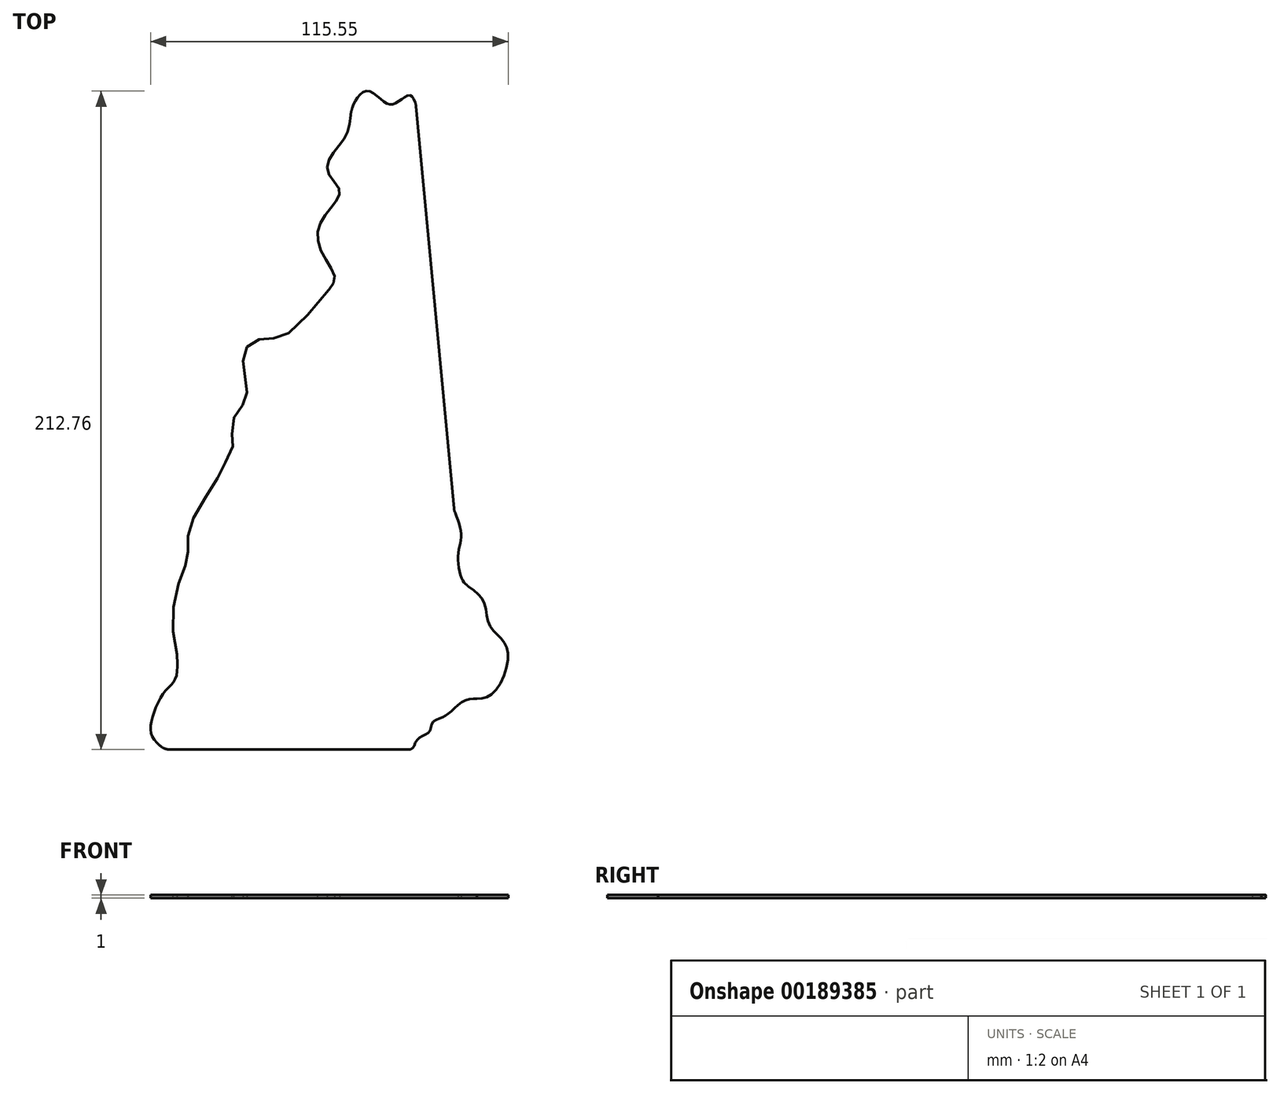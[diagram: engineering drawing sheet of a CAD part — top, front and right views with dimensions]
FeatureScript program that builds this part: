
annotation { "Feature Type Name" : "Feature", "Feature Type Description" : "" }
export const myFeature = defineFeature(function(context is Context, id is Id, definition is map)
    precondition{}
    {
        {
            var Q0;
            Q0=qCreatedBy(makeId("Top.planeOp"),FACE);
            var sketch = newSketch(context, id + "F0", { "sketchPlane" : qUnion([Q0])});
            skLineSegment(sketch, "E0.bottom", {"start": v(114, -114) * mm, "end": v(-114, -114) * mm});
            skLineSegment(sketch, "E0.top", {"start": v(114, 114) * mm, "end": v(-114, 114) * mm});
            skLineSegment(sketch, "E0.left", {"start": v(114, -114) * mm, "end": v(114, 114) * mm});
            skLineSegment(sketch, "E0.right", {"start": v(-114, -114) * mm, "end": v(-114, 114) * mm});
            skPoint(sketch, "E0.middle", {"position": v(0, 0) * mm});
            skSolve(sketch);
        }
        {
            var Q0;
            Q0 = qSketchRegion(id + "F0", true);
            extrude(context, id + "F1", {"entities" : qUnion([Q0]), "depth" : 1 * mm});
        }
        {
            var Q0;
            Q0=makeQuery(id+"F1.opExtrude","CAP_FACE",FACE,{"disambiguationData":[OSD([sQuery(id+"F0.wireOp",EDGE,"E0.bottom"),sQuery(id+"F0.wireOp",EDGE,"E0.top"),sQuery(id+"F0.wireOp",EDGE,"E0.left"),sQuery(id+"F0.wireOp",EDGE,"E0.right")])],"isStart":false});
            var sketch = newSketch(context, id + "F2", { "sketchPlane" : qUnion([Q0])});
            skLineSegment(sketch, "E1", {"start": v(29.36, 101.38) * mm, "end": v(41.77, -29.93) * mm});
            skFitSpline(sketch, "E2", {"points": [v(41.77, -29.93) * mm, v(44.03, -37.86) * mm, v(43.07, -44.1) * mm, v(44.29, -52) * mm, v(46.1, -54.26) * mm], "startDerivative": vector(11.5, -28.7) * mm, "endDerivative": vector(11.3, -9.92) * mm});
            skFitSpline(sketch, "E3", {"points": [v(46.1, -54.26) * mm, v(51.34, -59.36) * mm, v(52.94, -66.48) * mm, v(57.11, -71.39) * mm, v(59.2, -77.28) * mm, v(54.29, -88.93) * mm, v(49.14, -90.65) * mm], "startDerivative": vector(38.92, -26.66) * mm, "endDerivative": vector(-36.96, -2.14) * mm});
            skFitSpline(sketch, "E4", {"points": [v(49.14, -90.65) * mm, v(44.77, -91.48) * mm, v(40.29, -95.2) * mm, v(37.45, -96.83) * mm, v(34.71, -98.47) * mm, v(33.73, -101.31) * mm, v(31.1, -102.85) * mm, v(29.14, -105.03) * mm, v(28.48, -107.1) * mm], "startDerivative": vector(-31, -0.8) * mm, "endDerivative": vector(-4.65, -20.66) * mm});
            skLineSegment(sketch, "E5", {"start": v(28.48, -107.1) * mm, "end": v(-51.87, -107.1) * mm});
            skFitSpline(sketch, "E6", {"points": [v(-51.87, -107.1) * mm, v(-55.84, -102.73) * mm, v(-55.84, -96.95) * mm, v(-51.87, -88.49) * mm, v(-48.41, -84.36) * mm, v(-47.8, -76.72) * mm], "startDerivative": vector(-25.94, 21.9) * mm, "endDerivative": vector(-1.75, 40.4) * mm});
            skFitSpline(sketch, "E7", {"points": [v(-47.8, -76.72) * mm, v(-49.19, -63.8) * mm, v(-46.46, -50.93) * mm, v(-44.38, -45.2) * mm, v(-44.38, -40) * mm, v(-42.64, -32.56) * mm, v(-35.82, -21.26) * mm, v(-32.12, -14.25) * mm, v(-29.59, -8.02) * mm, v(-30.17, -4.7) * mm, v(-28.61, 1.92) * mm, v(-25.78, 5.3) * mm, v(-25.31, 10.56) * mm, v(-26.4, 16.44) * mm, v(-25.93, 21.7) * mm, v(-22.53, 25.1) * mm, v(-17.58, 25.72) * mm, v(-12.32, 27.1) * mm, v(1.28, 41.49) * mm], "startDerivative": vector(-32.3, 169.62) * mm, "endDerivative": vector(162.27, 198.26) * mm});
            skFitSpline(sketch, "E8", {"points": [v(1.28, 41.49) * mm, v(3.15, 45.36) * mm, v(0, 51.58) * mm, v(-2.42, 59.28) * mm, v(0, 65.5) * mm, v(3.64, 70.26) * mm, v(4.62, 74.02) * mm, v(1.28, 78.61) * mm, v(1.28, 83.36) * mm, v(4.79, 88.28) * mm, v(7.4, 92.86) * mm, v(8.4, 98.92) * mm], "startDerivative": vector(36.64, 46.8) * mm, "endDerivative": vector(6.08, 67.62) * mm});
            skFitSpline(sketch, "E9", {"points": [v(8.4, 98.92) * mm, v(10.36, 103.35) * mm, v(13.96, 105.64) * mm, v(18.88, 102.36) * mm, v(21.82, 101.38) * mm, v(25.26, 103.35) * mm, v(27.72, 104.16) * mm, v(29.36, 101.38) * mm], "startDerivative": vector(9.52, 28.83) * mm, "endDerivative": vector(10.47, -28.68) * mm});
            skLineSegment(sketch, "E10.bottom", {"start": v(135, 135) * mm, "end": v(-135, 135) * mm});
            skLineSegment(sketch, "E10.top", {"start": v(135, -135) * mm, "end": v(-135, -135) * mm});
            skLineSegment(sketch, "E10.left", {"start": v(135, 135) * mm, "end": v(135, -135) * mm});
            skLineSegment(sketch, "E10.right", {"start": v(-135, 135) * mm, "end": v(-135, -135) * mm});
            skPoint(sketch, "E10.middle", {"position": v(0, 0) * mm});
            skSolve(sketch);
        }
        {
            var Q0;
            Q0 = qSketchRegion(id + "F2", true);
            extrude(context, id + "F3", {"entities" : qUnion([Q0]), "operationType" : NewBodyOperationType.REMOVE, "endBound" : BoundingType.THROUGH_ALL, "oppositeDirection" : true, "depth" : 25 * mm});
        }
        {
            var Q0;
            Q0=makeQuery(id+"F3.boolean.opBoolean","COPY",EDGE,{"derivedFrom":makeQuery(id+"F3.opExtrude","SWEPT_EDGE",EDGE,{"disambiguationData":[OSD([sQuery(id+"F2.wireOp",EDGE,"E5"),sQuery(id+"F2.wireOp",EDGE,"E6")])]})});
            fillet(context, id + "F4", {"entities" : qUnion([Q0]), "radius" : 5 * mm, "tangentPropagation" : true, "allowEdgeOverflow" : false});
        }
        {
            var Q0;
            Q0=makeQuery(id+"F3.boolean.opBoolean","COPY",EDGE,{"derivedFrom":makeQuery(id+"F3.opExtrude","SWEPT_EDGE",EDGE,{"disambiguationData":[OSD([sQuery(id+"F2.wireOp",EDGE,"E4"),sQuery(id+"F2.wireOp",EDGE,"E5")])]})});
            fillet(context, id + "F5", {"entities" : qUnion([Q0]), "radius" : 2 * mm, "tangentPropagation" : true, "allowEdgeOverflow" : false});
        }
        {
            var Q0;
            Q0=makeQuery(id+"F3.boolean.opBoolean","COPY",EDGE,{"derivedFrom":makeQuery(id+"F3.opExtrude","SWEPT_EDGE",EDGE,{"disambiguationData":[OSD([sQuery(id+"F2.wireOp",EDGE,"E2"),sQuery(id+"F2.wireOp",EDGE,"E3")])]})});
            var Q1;
            Q1=makeQuery(id+"F3.boolean.opBoolean","COPY",EDGE,{"derivedFrom":makeQuery(id+"F3.opExtrude","SWEPT_EDGE",EDGE,{"disambiguationData":[OSD([sQuery(id+"F2.wireOp",EDGE,"E1"),sQuery(id+"F2.wireOp",EDGE,"E2")])]})});
            fillet(context, id + "F6", {"entities" : qUnion([Q0, Q1]), "radius" : 5 * mm, "tangentPropagation" : true, "allowEdgeOverflow" : false});
        }
        {
            var Q0;
            Q0=makeQuery(id+"F3.boolean.opBoolean","COPY",EDGE,{"derivedFrom":makeQuery(id+"F3.opExtrude","SWEPT_EDGE",EDGE,{"disambiguationData":[OSD([sQuery(id+"F2.wireOp",EDGE,"E1"),sQuery(id+"F2.wireOp",EDGE,"E9")])]})});
            fillet(context, id + "F7", {"entities" : qUnion([Q0]), "radius" : 5 * mm, "tangentPropagation" : true, "allowEdgeOverflow" : false});
        }
        {
            var Q0;
            Q0=makeQuery(id+"F3.boolean.opBoolean","COPY",EDGE,{"derivedFrom":makeQuery(id+"F3.opExtrude","SWEPT_EDGE",EDGE,{"disambiguationData":[OSD([sQuery(id+"F2.wireOp",EDGE,"E8"),sQuery(id+"F2.wireOp",EDGE,"E9")])]})});
            var Q1;
            Q1=makeQuery(id+"F3.boolean.opBoolean","COPY",EDGE,{"derivedFrom":makeQuery(id+"F3.opExtrude","SWEPT_EDGE",EDGE,{"disambiguationData":[OSD([sQuery(id+"F2.wireOp",EDGE,"E7"),sQuery(id+"F2.wireOp",EDGE,"E8")])]})});
            fillet(context, id + "F8", {"entities" : qUnion([Q0, Q1]), "radius" : 10 * mm, "tangentPropagation" : true, "allowEdgeOverflow" : false});
        }
        {
            var Q0;
            Q0=makeQuery(id+"F3.boolean.opBoolean","COPY",EDGE,{"derivedFrom":makeQuery(id+"F3.opExtrude","SWEPT_EDGE",EDGE,{"disambiguationData":[OSD([sQuery(id+"F2.wireOp",EDGE,"E6"),sQuery(id+"F2.wireOp",EDGE,"E7")])]})});
            fillet(context, id + "F9", {"entities" : qUnion([Q0]), "radius" : 5 * mm, "tangentPropagation" : true, "allowEdgeOverflow" : false});
        }
    });
